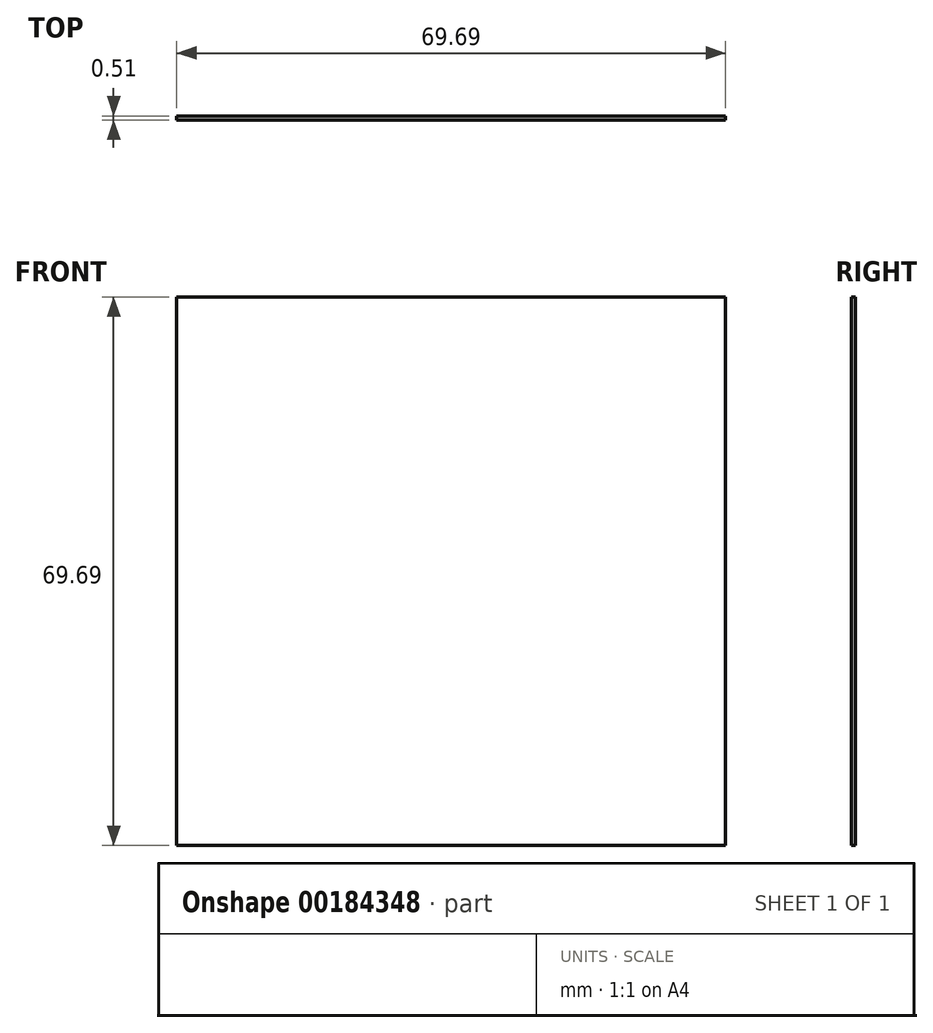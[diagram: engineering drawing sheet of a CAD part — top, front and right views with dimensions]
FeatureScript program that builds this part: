
annotation { "Feature Type Name" : "Feature", "Feature Type Description" : "" }
export const myFeature = defineFeature(function(context is Context, id is Id, definition is map)
    precondition{}
    {
        {
            var Q0;
            Q0=qCreatedBy(makeId("Front.planeOp"),FACE);
            var sketch = newSketch(context, id + "F0", { "sketchPlane" : qUnion([Q0])});
            skLineSegment(sketch, "E0.bottom", {"start": v(-30.2, 49.04) * mm, "end": v(39.49, 49.04) * mm});
            skLineSegment(sketch, "E0.top", {"start": v(-30.2, -20.65) * mm, "end": v(39.49, -20.65) * mm});
            skLineSegment(sketch, "E0.left", {"start": v(-30.2, 49.04) * mm, "end": v(-30.2, -20.65) * mm});
            skLineSegment(sketch, "E0.right", {"start": v(39.49, 49.04) * mm, "end": v(39.49, -20.65) * mm});
            skSolve(sketch);
        }
        {
            var Q0;
            Q0 = qSketchRegion(id + "F0", true);
            extrude(context, id + "F1", {"entities" : qUnion([Q0]), "depth" : 0.5 * mm});
        }
    });
